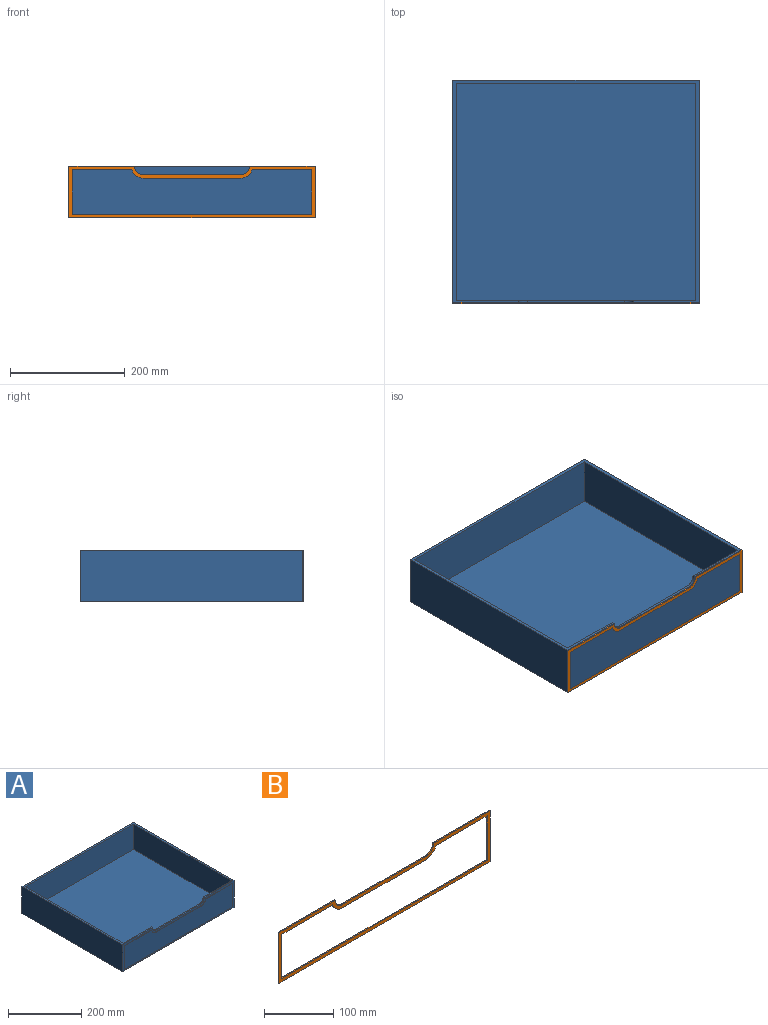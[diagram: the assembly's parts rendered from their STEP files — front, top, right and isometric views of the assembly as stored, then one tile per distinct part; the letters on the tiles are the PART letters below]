
ASSEMBLY  parts=2 mates=1
PART A: 23 faces, bbox 430x390x90 mm
  f0: plane 430x388mm, normal (0,0,-1), area 166840mm2, adj f5,f6,f7,f21
  f1: plane 430x388mm, normal (0,0,1), area 8036mm2, adj f2,f4,f5,f6,f7,f8,f9,f10
  f2: cylinder r=15mm len=15mm, axis (0,-1,0), area 94.2mm2, adj f1,f3,f9,f21
  f3: plane 170x4mm, normal (0,0,1), area 680mm2, adj f2,f4,f9,f21
  f4: cylinder r=15mm len=15mm, axis (0,-1,0), area 94.2mm2, adj f1,f3,f9,f21
  f5: plane 388x90mm, normal (-1,0,0), area 34920mm2, adj f0,f1,f7,f21
  f6: plane 388x90mm, normal (1,0,0), area 34920mm2, adj f0,f1,f7,f21
  f7: plane 430x90mm, normal (0,1,0), area 38700mm2, adj f0,f1,f5,f6
  f8: plane 378x84mm, normal (1,0,0), area 31752mm2, adj f1,f9,f11,f12
  f9: plane 418x84mm, normal (0,1,0), area 32208.6mm2, adj f1,f2,f3,f4,f8,f10,f12
  f10: plane 378x84mm, normal (-1,0,0), area 31752mm2, adj f1,f9,f11,f12
  f11: plane 418x84mm, normal (0,-1,0), area 35112mm2, adj f1,f8,f10,f12
  f12: plane 418x378mm, normal (0,0,1), area 158004mm2, adj f8,f9,f10,f11
  f13: plane 103.88x2mm, normal (0,0,1), area 207.8mm2, adj f14,f20,f21,f22
  f14: cylinder r=21mm len=20.12mm, axis (0,-1,0), area 53.8mm2, adj f13,f15,f21,f22
  f15: plane 170x2mm, normal (0,0,1), area 340mm2, adj f14,f16,f21,f22
  f16: cylinder r=21mm len=20.12mm, axis (0,-1,0), area 53.8mm2, adj f15,f17,f21,f22
  f17: plane 103.88x2mm, normal (0,0,1), area 207.8mm2, adj f16,f18,f21,f22
  f18: plane 78x2mm, normal (1,0,0), area 156mm2, adj f17,f19,f21,f22
  f19: plane 418x2mm, normal (0,0,-1), area 836mm2, adj f18,f20,f21,f22
  f20: plane 78x2mm, normal (-1,0,0), area 156mm2, adj f13,f19,f21,f22
  f21: plane 430x90mm, normal (0,-1,0), area 6186.8mm2, adj f0,f1,f2,f3,f4,f5,f6,f13
  f22: plane 418x78mm, normal (0,-1,0), area 29609.8mm2, adj f13,f14,f15,f16,f17,f18,f19,f20
PART B: 18 faces, bbox 430x2x90 mm
  f0: cylinder r=15mm len=15mm, axis (0,1,0), area 47.1mm2, adj f1,f15,f16,f17
  f1: plane 115x2mm, normal (0,0,1), area 230mm2, adj f0,f2,f16,f17
  f2: plane 90x2mm, normal (-1,0,0), area 180mm2, adj f1,f3,f16,f17
  f3: plane 430x2mm, normal (0,0,-1), area 860mm2, adj f2,f4,f16,f17
  f4: plane 90x2mm, normal (1,0,0), area 180mm2, adj f3,f5,f16,f17
  f5: plane 115x2mm, normal (0,0,1), area 230mm2, adj f4,f6,f16,f17
  f6: cylinder r=15mm len=15mm, axis (0,1,0), area 47.1mm2, adj f5,f15,f16,f17
  f7: plane 103.88x2mm, normal (0,0,-1), area 207.8mm2, adj f8,f14,f16,f17
  f8: cylinder r=21mm len=20.12mm, axis (0,1,0), area 53.8mm2, adj f7,f9,f16,f17
  f9: plane 170x2mm, normal (0,0,-1), area 340mm2, adj f8,f10,f16,f17
  f10: cylinder r=21mm len=20.12mm, axis (0,1,0), area 53.8mm2, adj f9,f11,f16,f17
  f11: plane 103.88x2mm, normal (0,0,-1), area 207.8mm2, adj f10,f12,f16,f17
  f12: plane 78x2mm, normal (-1,0,0), area 156mm2, adj f11,f13,f16,f17
  f13: plane 418x2mm, normal (0,0,1), area 836mm2, adj f12,f14,f16,f17
  f14: plane 78x2mm, normal (1,0,0), area 156mm2, adj f7,f13,f16,f17
  f15: plane 170x2mm, normal (0,0,1), area 340mm2, adj f0,f6,f16,f17
  f16: plane 430x90mm, normal (0,-1,0), area 6186.8mm2, adj f0,f1,f2,f3,f4,f5,f6,f7
  f17: plane 430x90mm, normal (0,1,0), area 6186.8mm2, adj f0,f1,f2,f3,f4,f5,f6,f7
PLACE A t=(2.17,62.79,47.31)mm
PLACE B t=(2.17,62.79,47.31)mm
MATE fastened B.f17 <-> A.f21  axis (0,1,0) through (217.17,-130.21,47.31)mm
